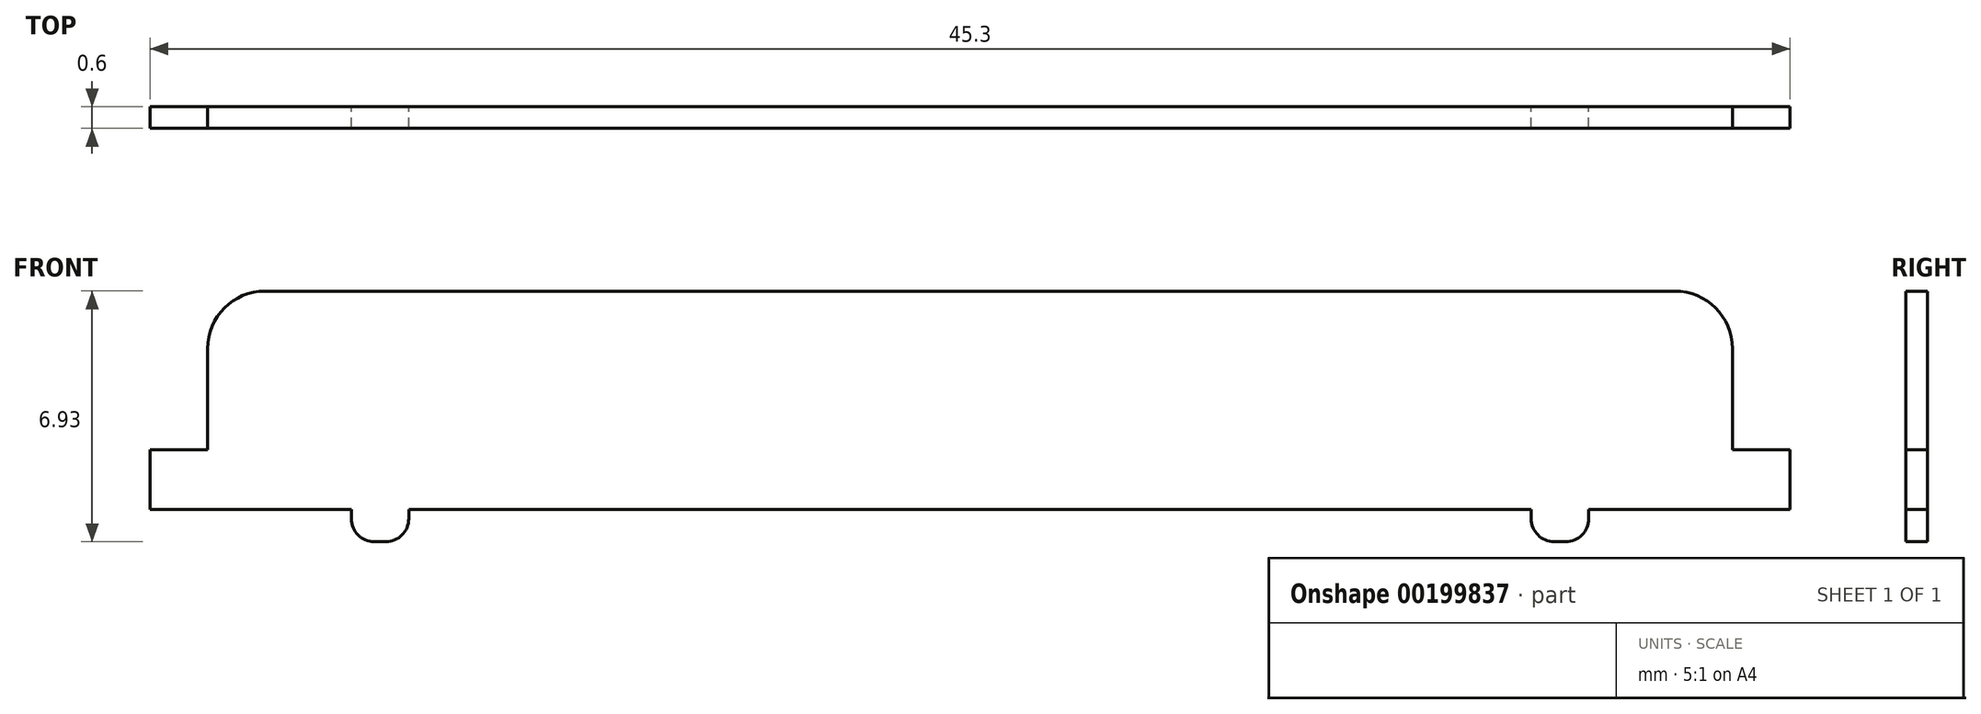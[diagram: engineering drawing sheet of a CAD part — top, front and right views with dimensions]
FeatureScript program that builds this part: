
annotation { "Feature Type Name" : "Feature", "Feature Type Description" : "" }
export const myFeature = defineFeature(function(context is Context, id is Id, definition is map)
    precondition{}
    {
        {
            assignVariable(context, id + "F0", {"name" : "fretwidth", "anyValue" : .6});
        }
        {
            var Q0;
            Q0=qCreatedBy(makeId("Front.planeOp"),FACE);
            var sketch = newSketch(context, id + "F1", { "sketchPlane" : qUnion([Q0])});
            skLineSegment(sketch, "E0", {"start": v(0, -3.2) * mm, "end": v(0, 3.25) * mm, "construction": true});
            skLineSegment(sketch, "E1", {"start": v(0, 0) * mm, "end": v(-15.5, 0) * mm});
            skLineSegment(sketch, "E2", {"start": v(-15.5, 0) * mm, "end": v(-15.5, -0.25) * mm});
            skLineSegment(sketch, "E3", {"start": v(-16.14, -0.89) * mm, "end": v(-16.46, -0.89) * mm});
            skLineSegment(sketch, "E4", {"start": v(-17.1, -0.25) * mm, "end": v(-17.1, 0) * mm});
            skLineSegment(sketch, "E5", {"start": v(-17.1, 0) * mm, "end": v(-22.65, 0) * mm});
            skLineSegment(sketch, "E6", {"start": v(-22.65, 0) * mm, "end": v(-22.65, 1.65) * mm});
            skLineSegment(sketch, "E7", {"start": v(-22.65, 1.65) * mm, "end": v(-21.06, 1.65) * mm});
            skLineSegment(sketch, "E8", {"start": v(-21.06, 1.65) * mm, "end": v(-21.06, 4.45) * mm});
            skLineSegment(sketch, "E9", {"start": v(-19.47, 6.04) * mm, "end": v(0, 6.04) * mm});
            skPoint(sketch, "E10.visualSharp", {"position": v(-21.06, 6.04) * mm});
            skArc(sketch, "E10.filletArc", {"start": v(-19.47, 6.04) * mm, "mid": v(-20.6, 5.57) * mm, "end": v(-21.06, 4.45) * mm});
            skPoint(sketch, "E11.visualSharp", {"position": v(-17.1, -0.89) * mm});
            skArc(sketch, "E11.filletArc", {"start": v(-17.1, -0.25) * mm, "mid": v(-16.9, -0.7) * mm, "end": v(-16.46, -0.89) * mm});
            skPoint(sketch, "E12.visualSharp", {"position": v(-15.5, -0.89) * mm});
            skArc(sketch, "E12.filletArc", {"start": v(-16.14, -0.89) * mm, "mid": v(-15.69, -0.7) * mm, "end": v(-15.5, -0.25) * mm});
            skLineSegment(sketch, "E13.MirrorCS", {"start": v(16.14, -0.89) * mm, "end": v(16.46, -0.89) * mm});
            skLineSegment(sketch, "E14.MirrorCS", {"start": v(15.5, 0) * mm, "end": v(15.5, -0.25) * mm});
            skLineSegment(sketch, "E15.MirrorCS", {"start": v(17.1, -0.25) * mm, "end": v(17.1, 0) * mm});
            skArc(sketch, "E16.MirrorCS", {"start": v(17.1, -0.25) * mm, "mid": v(16.9, -0.7) * mm, "end": v(16.46, -0.89) * mm});
            skArc(sketch, "E17.MirrorCS", {"start": v(16.14, -0.89) * mm, "mid": v(15.69, -0.7) * mm, "end": v(15.5, -0.25) * mm});
            skLineSegment(sketch, "E18.MirrorCS", {"start": v(19.47, 6.04) * mm, "end": v(0, 6.04) * mm});
            skLineSegment(sketch, "E19.MirrorCS", {"start": v(21.06, 1.65) * mm, "end": v(21.06, 4.45) * mm});
            skLineSegment(sketch, "E20.MirrorCS", {"start": v(22.65, 1.65) * mm, "end": v(21.06, 1.65) * mm});
            skLineSegment(sketch, "E21.MirrorCS", {"start": v(0, 0) * mm, "end": v(15.5, 0) * mm});
            skLineSegment(sketch, "E22.MirrorCS", {"start": v(22.65, 0) * mm, "end": v(22.65, 1.65) * mm});
            skPoint(sketch, "E23.MirrorP", {"position": v(15.5, -0.89) * mm});
            skArc(sketch, "E24.MirrorCS", {"start": v(19.47, 6.04) * mm, "mid": v(20.6, 5.57) * mm, "end": v(21.06, 4.45) * mm});
            skPoint(sketch, "E25.MirrorP", {"position": v(21.06, 6.04) * mm});
            skPoint(sketch, "E26.MirrorP", {"position": v(17.1, -0.89) * mm});
            skLineSegment(sketch, "E27.MirrorCS", {"start": v(17.1, 0) * mm, "end": v(22.65, 0) * mm});
            skLineSegment(sketch, "E28", {"start": v(-16.3, -0.55) * mm, "end": v(-16.3, -1.5) * mm, "construction": true});
            skPoint(sketch, "E28.startSnap0", {"position": v(-16.3, -0.89) * mm});
            skSolve(sketch);
        }
        {
            var Q0;
            Q0=qSketchRegion(id+"F1",true);
            extrude(context, id + "F2", {"entities" : qUnion([Q0]), "depth" : (getVariable(context, 'fretwidth')) * mm});
        }
    });
